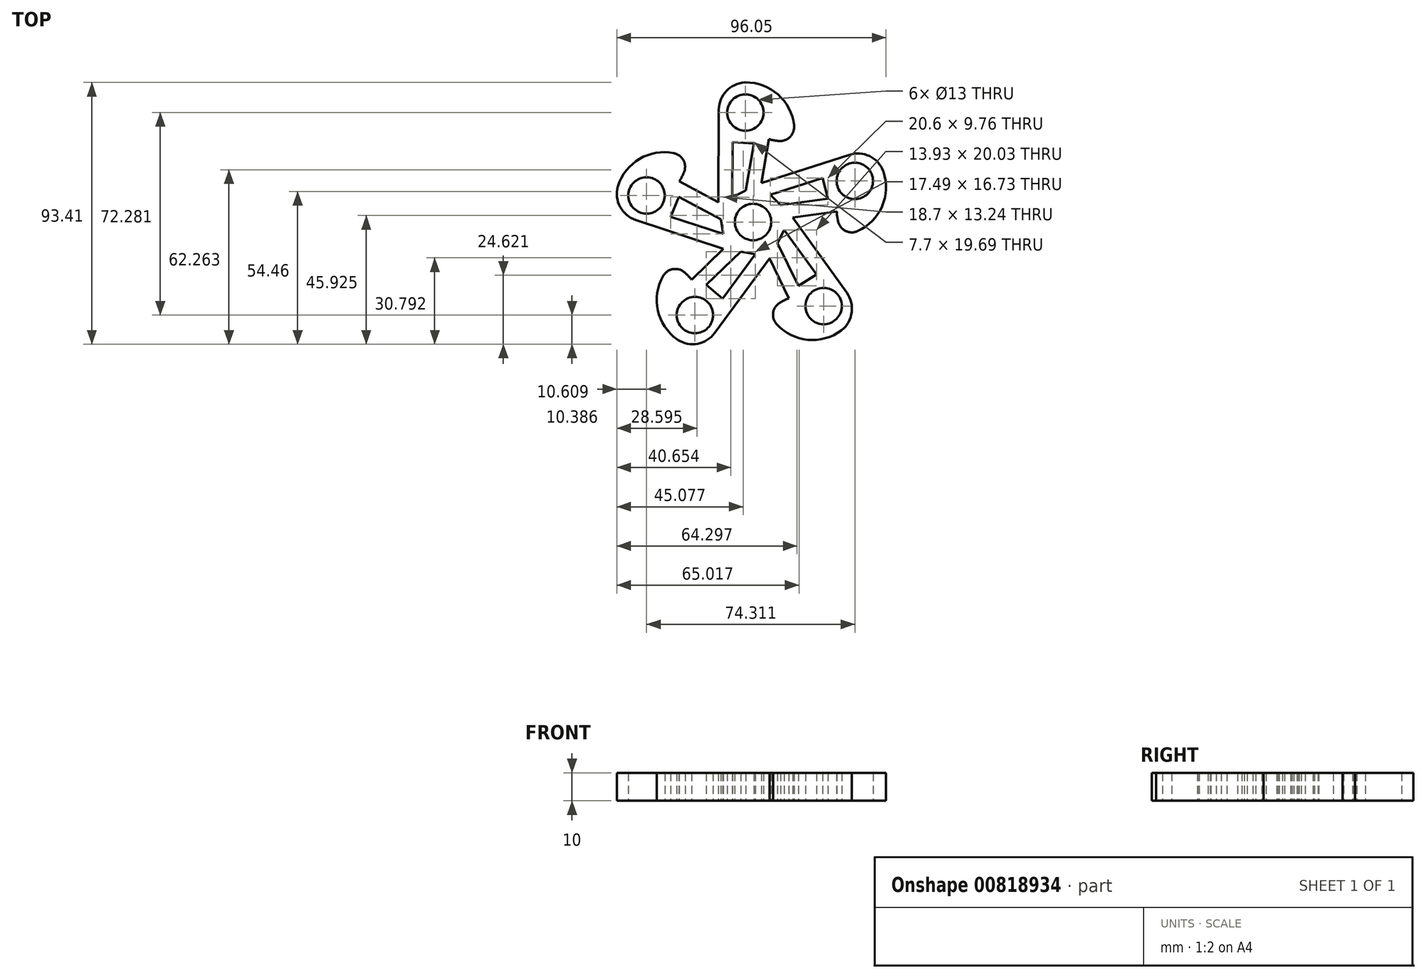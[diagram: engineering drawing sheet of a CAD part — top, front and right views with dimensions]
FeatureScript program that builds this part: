
annotation { "Feature Type Name" : "Feature", "Feature Type Description" : "" }
export const myFeature = defineFeature(function(context is Context, id is Id, definition is map)
    precondition{}
    {
        {
            var Q0;
            Q0=qCreatedBy(makeId("Top.planeOp"),FACE);
            var sketch = newSketch(context, id + "F0", { "sketchPlane" : qUnion([Q0])});
            skCircle(sketch, "E0", {"center": v(0, 0) * mm, "radius": 12.5 * mm});
            skSolve(sketch);
        }
        {
            var Q0;
            Q0=qCreatedBy(makeId("Top.planeOp"),FACE);
            var sketch = newSketch(context, id + "F1", { "sketchPlane" : qUnion([Q0])});
            skCircle(sketch, "E1", {"center": v(0, 0) * mm, "radius": 6.5 * mm});
            skSolve(sketch);
        }
        {
            var Q0;
            Q0 = qSketchRegion(id + "F0", true);
            extrude(context, id + "F2", {"entities" : qUnion([Q0]), "depth" : 10 * mm, "offsetDistance" : 25 * mm});
        }
        {
            var Q0;
            Q0=qCreatedBy(makeId("Top.planeOp"),FACE);
            var sketch = newSketch(context, id + "F3", { "sketchPlane" : qUnion([Q0])});
            skLineSegment(sketch, "E2.left", {"start": v(-5.08, 11.42) * mm, "end": v(34.33, 24.01) * mm});
            skLineSegment(sketch, "E2.right", {"start": v(12.43, 1.3) * mm, "end": v(29.84, 3.74) * mm});
            skArc(sketch, "E3", {"start": v(46.45, 18.2) * mm, "mid": v(41.54, 23.52) * mm, "end": v(34.33, 24.01) * mm});
            skArc(sketch, "E4", {"start": v(29.84, 3.74) * mm, "mid": v(30.02, 1.92) * mm, "end": v(30.36, 0.13) * mm});
            skPoint(sketch, "E5", {"position": v(29.84, 3.74) * mm});
            skArc(sketch, "E6", {"start": v(37.28, -3.27) * mm, "mid": v(46.02, 5.59) * mm, "end": v(46.52, 18.02) * mm});
            skPoint(sketch, "E7.visualSharp", {"position": v(46.81, 17.08) * mm});
            skArc(sketch, "E7.filletArc", {"start": v(46.52, 18.02) * mm, "mid": v(46.49, 18.11) * mm, "end": v(46.45, 18.2) * mm});
            skPoint(sketch, "E8.visualSharp", {"position": v(32.2, -4.67) * mm});
            skArc(sketch, "E8.filletArc", {"start": v(30.36, 0.13) * mm, "mid": v(33.02, -3.2) * mm, "end": v(37.28, -3.27) * mm});
            skLineSegment(sketch, "E9.1.0", {"start": v(2.6, 12.23) * mm, "end": v(5.67, 29.54) * mm});
            skArc(sketch, "E9.1.1", {"start": v(14.63, 34.45) * mm, "mid": v(8.9, 45.5) * mm, "end": v(-2.76, 49.81) * mm});
            skArc(sketch, "E9.1.2", {"start": v(-2.96, 49.8) * mm, "mid": v(-9.53, 46.78) * mm, "end": v(-12.23, 40.07) * mm});
            skLineSegment(sketch, "E9.1.3", {"start": v(-12.43, -1.3) * mm, "end": v(-12.23, 40.07) * mm});
            skPoint(sketch, "E9.1.4", {"position": v(5.67, 29.54) * mm});
            skPoint(sketch, "E9.1.5", {"position": v(-1.78, 49.8) * mm});
            skPoint(sketch, "E9.1.6", {"position": v(14.4, 29.17) * mm});
            skArc(sketch, "E9.1.7", {"start": v(9.26, 28.92) * mm, "mid": v(13.24, 30.42) * mm, "end": v(14.63, 34.45) * mm});
            skArc(sketch, "E9.1.8", {"start": v(-2.76, 49.81) * mm, "mid": v(-2.86, 49.81) * mm, "end": v(-2.96, 49.8) * mm});
            skArc(sketch, "E9.1.9", {"start": v(5.67, 29.54) * mm, "mid": v(7.45, 29.14) * mm, "end": v(9.26, 28.92) * mm});
            skLineSegment(sketch, "E9.2.0", {"start": v(-10.82, 6.26) * mm, "end": v(-26.34, 14.52) * mm});
            skArc(sketch, "E9.2.1", {"start": v(-28.24, 24.56) * mm, "mid": v(-40.51, 22.53) * mm, "end": v(-48.23, 12.77) * mm});
            skArc(sketch, "E9.2.2", {"start": v(-48.28, 12.57) * mm, "mid": v(-47.43, 5.4) * mm, "end": v(-41.89, 0.75) * mm});
            skLineSegment(sketch, "E9.2.3", {"start": v(-2.6, -12.23) * mm, "end": v(-41.89, 0.75) * mm});
            skPoint(sketch, "E9.2.4", {"position": v(-26.34, 14.52) * mm});
            skPoint(sketch, "E9.2.5", {"position": v(-47.91, 13.7) * mm});
            skPoint(sketch, "E9.2.6", {"position": v(-23.3, 22.7) * mm});
            skArc(sketch, "E9.2.7", {"start": v(-24.64, 17.74) * mm, "mid": v(-24.84, 22) * mm, "end": v(-28.24, 24.56) * mm});
            skArc(sketch, "E9.2.8", {"start": v(-48.23, 12.77) * mm, "mid": v(-48.26, 12.67) * mm, "end": v(-48.28, 12.57) * mm});
            skArc(sketch, "E9.2.9", {"start": v(-26.34, 14.52) * mm, "mid": v(-25.42, 16.1) * mm, "end": v(-24.64, 17.74) * mm});
            skLineSegment(sketch, "E9.3.0", {"start": v(-9.3, -8.36) * mm, "end": v(-21.95, -20.56) * mm});
            skArc(sketch, "E9.3.1", {"start": v(-32.08, -19.27) * mm, "mid": v(-33.94, -31.57) * mm, "end": v(-27.04, -41.92) * mm});
            skArc(sketch, "E9.3.2", {"start": v(-26.88, -42.04) * mm, "mid": v(-19.79, -43.44) * mm, "end": v(-13.66, -39.6) * mm});
            skLineSegment(sketch, "E9.3.3", {"start": v(10.83, -6.25) * mm, "end": v(-13.66, -39.6) * mm});
            skPoint(sketch, "E9.3.4", {"position": v(-21.95, -20.56) * mm});
            skPoint(sketch, "E9.3.5", {"position": v(-27.83, -41.34) * mm});
            skPoint(sketch, "E9.3.6", {"position": v(-28.79, -15.14) * mm});
            skArc(sketch, "E9.3.7", {"start": v(-24.49, -17.95) * mm, "mid": v(-28.6, -16.82) * mm, "end": v(-32.08, -19.27) * mm});
            skArc(sketch, "E9.3.8", {"start": v(-27.04, -41.92) * mm, "mid": v(-26.96, -41.98) * mm, "end": v(-26.88, -42.04) * mm});
            skArc(sketch, "E9.3.9", {"start": v(-21.95, -20.56) * mm, "mid": v(-23.16, -19.2) * mm, "end": v(-24.49, -17.95) * mm});
            skLineSegment(sketch, "E9.4.0", {"start": v(5.08, -11.42) * mm, "end": v(12.77, -27.23) * mm});
            skArc(sketch, "E9.4.1", {"start": v(8.41, -36.46) * mm, "mid": v(19.54, -42.04) * mm, "end": v(31.51, -38.68) * mm});
            skArc(sketch, "E9.4.2", {"start": v(31.67, -38.55) * mm, "mid": v(35.2, -32.24) * mm, "end": v(33.45, -25.23) * mm});
            skLineSegment(sketch, "E9.4.3", {"start": v(9.29, 8.36) * mm, "end": v(33.45, -25.23) * mm});
            skPoint(sketch, "E9.4.4", {"position": v(12.77, -27.23) * mm});
            skPoint(sketch, "E9.4.5", {"position": v(30.71, -39.24) * mm});
            skPoint(sketch, "E9.4.6", {"position": v(5.5, -32.06) * mm});
            skArc(sketch, "E9.4.7", {"start": v(9.5, -28.84) * mm, "mid": v(7.17, -32.4) * mm, "end": v(8.41, -36.46) * mm});
            skArc(sketch, "E9.4.8", {"start": v(31.51, -38.68) * mm, "mid": v(31.6, -38.61) * mm, "end": v(31.67, -38.55) * mm});
            skArc(sketch, "E9.4.9", {"start": v(12.77, -27.23) * mm, "mid": v(11.1, -27.96) * mm, "end": v(9.5, -28.84) * mm});
            skPoint(sketch, "E9.center", {"position": v(0, 0) * mm});
            skCircle(sketch, "E10", {"center": v(36.31, 14.67) * mm, "radius": 6.5 * mm});
            skCircle(sketch, "E11.1.0", {"center": v(-2.73, 39.07) * mm, "radius": 6.5 * mm});
            skCircle(sketch, "E11.2.0", {"center": v(-38, 9.47) * mm, "radius": 6.5 * mm});
            skCircle(sketch, "E11.3.0", {"center": v(-20.75, -33.21) * mm, "radius": 6.5 * mm});
            skCircle(sketch, "E11.4.0", {"center": v(25.18, -30) * mm, "radius": 6.5 * mm});
            skSolve(sketch);
        }
        {
            var Q0;
            {var subQ12=sQuery(id+"F3.wireOp",EDGE,"E3");Q0=makeQuery(id+"F3.imprint","IMPRINT",FACE,{"disambiguationData":[TD([[makeQuery(id+"F3.imprint","IMPRINT",EDGE,{"derivedFrom":subQ12}),1.0]])]});}
            extrude(context, id + "F4", {"entities" : qUnion([Q0]), "operationType" : NewBodyOperationType.ADD, "depth" : 10 * mm, "offsetDistance" : 25 * mm});
        }
        {
            var Q0;
            Q0 = qSketchRegion(id + "F1", true);
            extrude(context, id + "F5", {"entities" : qUnion([Q0]), "operationType" : NewBodyOperationType.REMOVE, "depth" : 10 * mm, "offsetDistance" : 25 * mm});
        }
        {
            var Q0;
            Q0=qCreatedBy(makeId("Top.planeOp"),FACE);
            var sketch = newSketch(context, id + "F6", { "sketchPlane" : qUnion([Q0])});
            skLineSegment(sketch, "E12.bottom", {"start": v(-7.29, 28.5) * mm, "end": v(0.32, 27.98) * mm});
            skLineSegment(sketch, "E12.top", {"start": v(-7.38, 8.82) * mm, "end": v(-2.65, 11.19) * mm});
            skLineSegment(sketch, "E12.left", {"start": v(-7.29, 28.5) * mm, "end": v(-7.38, 8.82) * mm});
            skLineSegment(sketch, "E12.right", {"start": v(0.32, 27.98) * mm, "end": v(-2.65, 11.19) * mm});
            skLineSegment(sketch, "E13.1.0", {"start": v(-29.36, 1.88) * mm, "end": v(-26.51, 8.95) * mm});
            skLineSegment(sketch, "E13.1.1", {"start": v(-26.51, 8.95) * mm, "end": v(-11.46, 0.93) * mm});
            skLineSegment(sketch, "E13.1.2", {"start": v(-29.36, 1.88) * mm, "end": v(-10.67, -4.3) * mm});
            skLineSegment(sketch, "E13.1.3", {"start": v(-10.67, -4.3) * mm, "end": v(-11.46, 0.93) * mm});
            skLineSegment(sketch, "E13.2.0", {"start": v(-10.86, -27.35) * mm, "end": v(-16.7, -22.45) * mm});
            skLineSegment(sketch, "E13.2.1", {"start": v(-16.7, -22.45) * mm, "end": v(-4.43, -10.61) * mm});
            skLineSegment(sketch, "E13.2.2", {"start": v(-10.86, -27.35) * mm, "end": v(0.79, -11.47) * mm});
            skLineSegment(sketch, "E13.2.3", {"start": v(0.79, -11.47) * mm, "end": v(-4.43, -10.61) * mm});
            skLineSegment(sketch, "E13.3.0", {"start": v(22.65, -18.78) * mm, "end": v(16.2, -22.82) * mm});
            skLineSegment(sketch, "E13.3.1", {"start": v(16.2, -22.82) * mm, "end": v(8.72, -7.5) * mm});
            skLineSegment(sketch, "E13.3.2", {"start": v(22.65, -18.78) * mm, "end": v(11.16, -2.8) * mm});
            skLineSegment(sketch, "E13.3.3", {"start": v(11.16, -2.8) * mm, "end": v(8.72, -7.5) * mm});
            skLineSegment(sketch, "E13.4.0", {"start": v(24.86, 15.74) * mm, "end": v(26.7, 8.35) * mm});
            skLineSegment(sketch, "E13.4.1", {"start": v(26.7, 8.35) * mm, "end": v(9.82, 5.98) * mm});
            skLineSegment(sketch, "E13.4.2", {"start": v(24.86, 15.74) * mm, "end": v(6.1, 9.75) * mm});
            skLineSegment(sketch, "E13.4.3", {"start": v(6.1, 9.75) * mm, "end": v(9.82, 5.98) * mm});
            skPoint(sketch, "E13.center", {"position": v(0, 0) * mm});
            skSolve(sketch);
        }
        {
            var Q0;
            Q0 = qSketchRegion(id + "F6", true);
            extrude(context, id + "F7", {"entities" : qUnion([Q0]), "operationType" : NewBodyOperationType.REMOVE, "depth" : 10 * mm, "offsetDistance" : 25 * mm});
        }
    });
